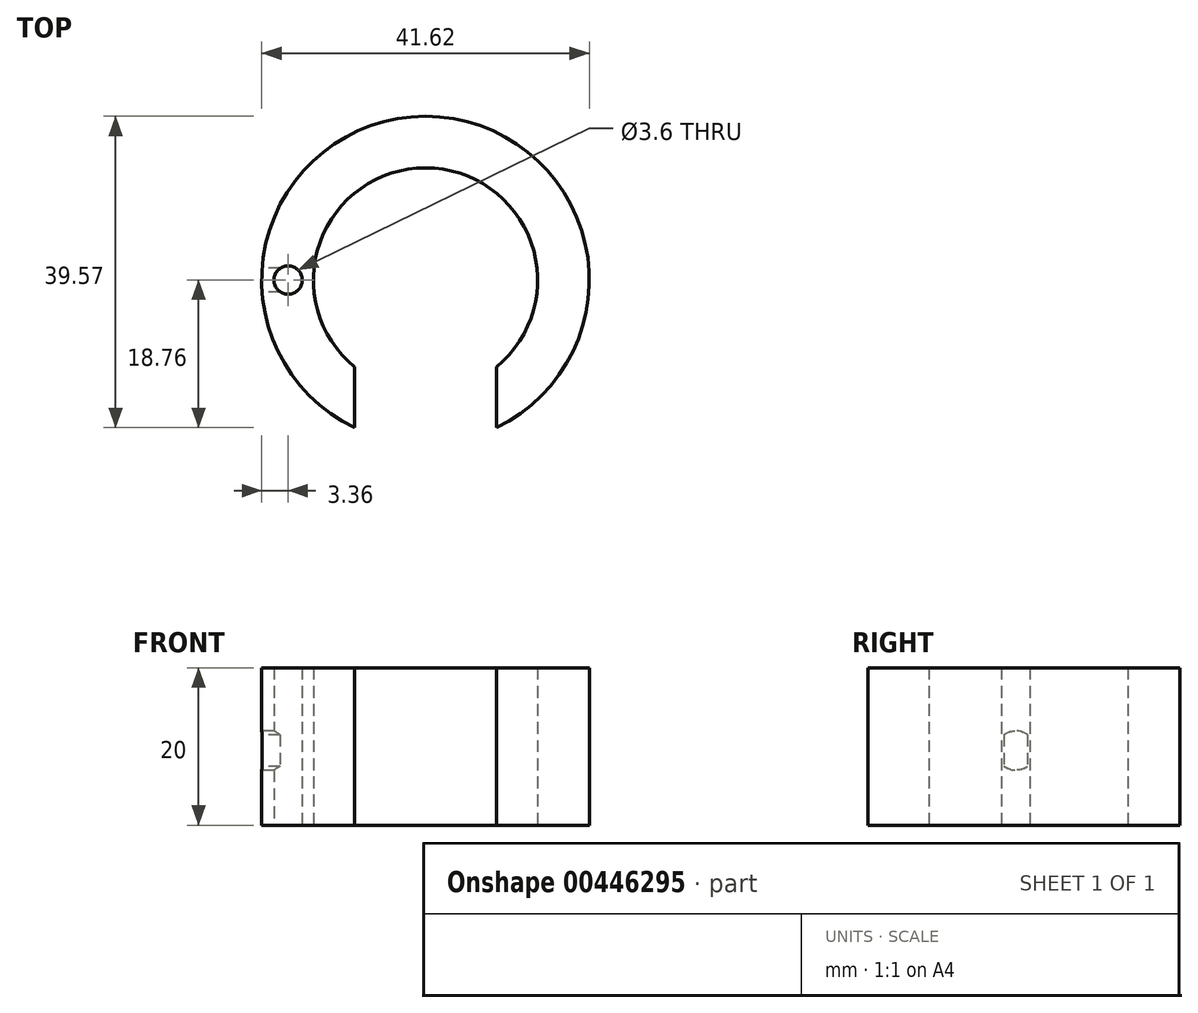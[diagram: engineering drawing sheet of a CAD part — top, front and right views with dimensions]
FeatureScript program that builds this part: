
annotation { "Feature Type Name" : "Feature", "Feature Type Description" : "" }
export const myFeature = defineFeature(function(context is Context, id is Id, definition is map)
    precondition{}
    {
        {
            var Q0;
            Q0=qCreatedBy(makeId("Top.planeOp"),FACE);
            var sketch = newSketch(context, id + "F0", { "sketchPlane" : qUnion([Q0])});
            skCircle(sketch, "E0", {"center": v(0, 0) * mm, "radius": 14.25 * mm});
            skCircle(sketch, "E1", {"center": v(0, 0) * mm, "radius": 20.8 * mm});
            skLineSegment(sketch, "E2", {"start": v(-9, -11.05) * mm, "end": v(9, -11.05) * mm});
            skLineSegment(sketch, "E3.top", {"start": v(-9, -31.52) * mm, "end": v(9, -31.52) * mm});
            skLineSegment(sketch, "E3.left", {"start": v(-9, -11.05) * mm, "end": v(-9, -31.52) * mm});
            skLineSegment(sketch, "E3.right", {"start": v(9, -11.05) * mm, "end": v(9, -31.52) * mm});
            skLineSegment(sketch, "E4", {"start": v(14.25, 0) * mm, "end": v(15.65, 0) * mm, "construction": true});
            skLineSegment(sketch, "E5", {"start": v(15.65, 0) * mm, "end": v(17.45, 0) * mm, "construction": true});
            skCircle(sketch, "E6", {"center": v(17.45, 0) * mm, "radius": 1.8 * mm});
            skLineSegment(sketch, "E7", {"start": v(0, 0) * mm, "end": v(0, -4.56) * mm, "construction": true});
            skCircle(sketch, "E8.MirrorC", {"center": v(-17.45, 0) * mm, "radius": 1.8 * mm});
            skPoint(sketch, "E9", {"position": v(-20.8, 0) * mm});
            skSolve(sketch);
        }
        {
            var Q0;
            {var subQ0=sQuery(id+"F0.wireOp",EDGE,"E3.left");var subQ6=sQuery(id+"F0.wireOp",EDGE,"E1");var subQ7=makeQuery(id+"F0.imprint","INTERSECT",VERTEX,{"derivedFrom":[subQ6,subQ0]});Q0=makeQuery(id+"F0.imprint","IMPRINT",FACE,{"disambiguationData":[TD([[makeQuery(id+"F0.imprint","IMPRINT",EDGE,{"disambiguationData":[TD([[subQ7,1.0]])],"derivedFrom":subQ6}),1.0]])]});}
            var Q1;
            Q1=makeQuery(id+"F0.imprint","IMPRINT",FACE,{"disambiguationData":[TD([[makeQuery(id+"F0.imprint","IMPRINT",EDGE,{"derivedFrom":sQuery(id+"F0.wireOp",EDGE,"E6")}),1.0]])]});
            var Q2;
            Q2=makeQuery(id+"F0.imprint","IMPRINT",FACE,{"disambiguationData":[TD([[makeQuery(id+"F0.imprint","IMPRINT",EDGE,{"derivedFrom":sQuery(id+"F0.wireOp",EDGE,"E8.MirrorC")}),-1.0]])]});
            extrude(context, id + "F1", {"entities" : qUnion([Q0, Q1, Q2]), "depth" : 17 * mm});
        }
        {
            var Q0;
            Q0=makeQuery(id+"F0.imprint","IMPRINT",FACE,{"disambiguationData":[TD([[makeQuery(id+"F0.imprint","IMPRINT",EDGE,{"derivedFrom":sQuery(id+"F0.wireOp",EDGE,"E6")}),1.0]])]});
            var Q1;
            Q1=makeQuery(id+"F0.imprint","IMPRINT",FACE,{"disambiguationData":[TD([[makeQuery(id+"F0.imprint","IMPRINT",EDGE,{"derivedFrom":sQuery(id+"F0.wireOp",EDGE,"E8.MirrorC")}),-1.0]])]});
            extrude(context, id + "F2", {"entities" : qUnion([Q0, Q1]), "operationType" : NewBodyOperationType.ADD, "depth" : 20 * mm});
        }
        {
            var Q0;
            Q0=qCreatedBy(makeId("Right.planeOp"),FACE);
            var Q1;
            Q1=sQuery(id+"F0.wireOp",VERTEX,"E9");
            cPlane(context, id + "F3", {"entities" : qUnion([Q0, Q1]), "cplaneType" : CPlaneType.PLANE_POINT, "offset" : 25 * mm, "width" : 150 * mm, "height" : 150 * mm});
        }
        {
            var Q0;
            Q0=qCreatedBy(id+"F3.planeOp",FACE);
            var sketch = newSketch(context, id + "F4", { "sketchPlane" : qUnion([Q0])});
            skLineSegment(sketch, "E10", {"start": v(0, 0) * mm, "end": v(0, 9.5) * mm, "construction": true});
            skPoint(sketch, "E11.middle", {"position": v(0, 9.5) * mm});
            skCircle(sketch, "E12", {"center": v(0, 9.5) * mm, "radius": 2.5 * mm});
            skLineSegment(sketch, "E13.bottom", {"start": v(-1.5, 13.45) * mm, "end": v(1.5, 13.45) * mm});
            skLineSegment(sketch, "E13.top", {"start": v(-1.5, 5.55) * mm, "end": v(1.5, 5.55) * mm});
            skLineSegment(sketch, "E13.left", {"start": v(-1.5, 13.45) * mm, "end": v(-1.5, 5.55) * mm});
            skLineSegment(sketch, "E13.right", {"start": v(1.5, 13.45) * mm, "end": v(1.5, 5.55) * mm});
            skSolve(sketch);
        }
        {
            var Q0;
            {var subQ0=sQuery(id+"F4.wireOp",EDGE,"E13.left");var subQ1=sQuery(id+"F4.wireOp",EDGE,"E12");var subQ2=makeQuery(id+"F4.imprint","INTERSECT",VERTEX,{"disambiguationData":[OD(0.0)],"derivedFrom":[subQ1,subQ0]});Q0=makeQuery(id+"F4.imprint","IMPRINT",FACE,{"disambiguationData":[TD([[makeQuery(id+"F4.imprint","IMPRINT",EDGE,{"disambiguationData":[TD([[subQ2,1.0]])],"derivedFrom":subQ1}),1.0]])]});}
            extrude(context, id + "F5", {"entities" : qUnion([Q0]), "operationType" : NewBodyOperationType.REMOVE, "endBound" : BoundingType.UP_TO_NEXT, "depth" : 25 * mm});
        }
    });
